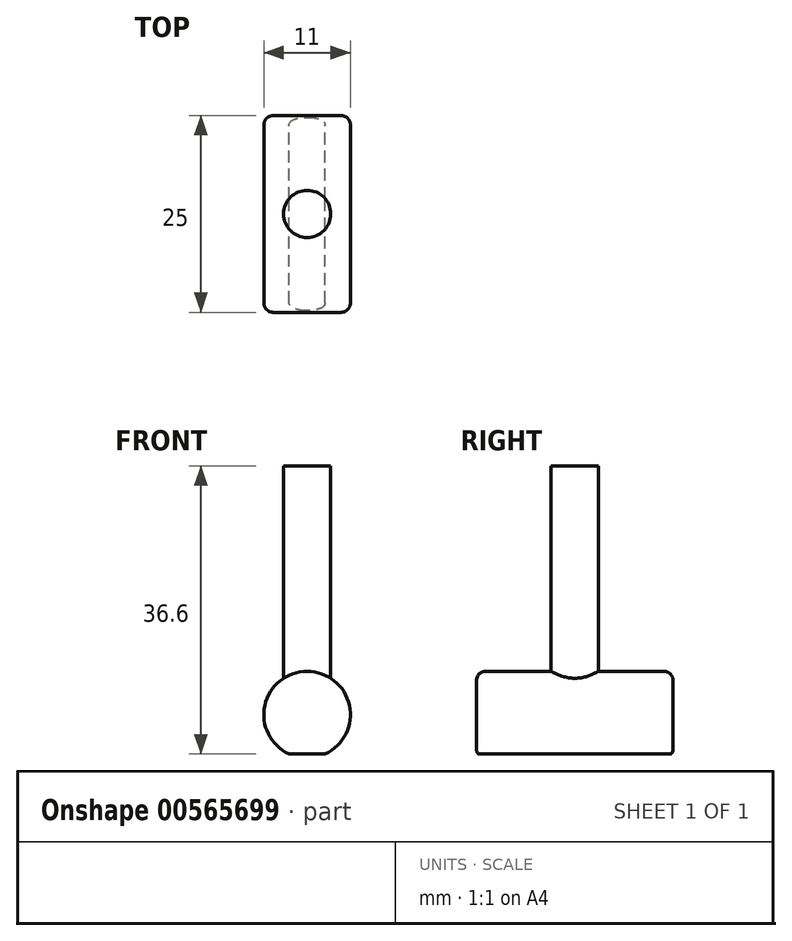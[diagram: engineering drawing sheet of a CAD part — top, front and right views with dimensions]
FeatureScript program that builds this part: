
annotation { "Feature Type Name" : "Feature", "Feature Type Description" : "" }
export const myFeature = defineFeature(function(context is Context, id is Id, definition is map)
    precondition{}
    {
        {
            var Q0;
            Q0=qCreatedBy(makeId("Front.planeOp"),FACE);
            var sketch = newSketch(context, id + "F0", { "sketchPlane" : qUnion([Q0])});
            skCircle(sketch, "E0", {"center": v(0, 0) * mm, "radius": 5.5 * mm});
            skSolve(sketch);
        }
        {
            var Q0;
            Q0 = qSketchRegion(id + "F0", true);
            extrude(context, id + "F1", {"entities" : qUnion([Q0]), "depth" : 25 * mm, "offsetDistance" : 25 * mm});
        }
        {
            var Q0;
            Q0=qCreatedBy(makeId("Front.planeOp"),FACE);
            var sketch = newSketch(context, id + "F2", { "sketchPlane" : qUnion([Q0])});
            skLineSegment(sketch, "E1", {"start": v(0, 11.6) * mm, "end": v(0, -5.5) * mm, "construction": true});
            skLineSegment(sketch, "E2.bottom", {"start": v(-2.3, -5) * mm, "end": v(2.3, -5) * mm});
            skLineSegment(sketch, "E2.top", {"start": v(-2.3, -5.5) * mm, "end": v(2.3, -5.5) * mm});
            skLineSegment(sketch, "E2.left", {"start": v(-2.3, -5) * mm, "end": v(-2.3, -5.5) * mm});
            skLineSegment(sketch, "E2.right", {"start": v(2.3, -5) * mm, "end": v(2.3, -5.5) * mm});
            skSolve(sketch);
        }
        {
            var Q0;
            Q0 = qSketchRegion(id + "F2", true);
            extrude(context, id + "F3", {"entities" : qUnion([Q0]), "operationType" : NewBodyOperationType.REMOVE, "endBound" : BoundingType.THROUGH_ALL, "depth" : 25 * mm, "offsetDistance" : 25 * mm});
        }
        {
            var Q0;
            Q0=sQuery(id+"F2.wireOp",VERTEX,"E1.start");
            var Q1;
            Q1=makeQuery(id+"F3.boolean.opBoolean","COPY",FACE,{"derivedFrom":makeQuery(id+"F3.opExtrude","SWEPT_FACE",FACE,{"disambiguationData":[OSD([sQuery(id+"F2.wireOp",EDGE,"E2.bottom")])]})});
            cPlane(context, id + "F4", {"entities" : qUnion([Q0, Q1]), "cplaneType" : CPlaneType.PLANE_POINT, "offset" : 25 * mm, "width" : 150 * mm, "height" : 150 * mm});
        }
        {
            var Q0;
            Q0=qCreatedBy(id+"F4.planeOp",FACE);
            var sketch = newSketch(context, id + "F5", { "sketchPlane" : qUnion([Q0])});
            skCircle(sketch, "E3", {"center": v(0, 12.5) * mm, "radius": 3 * mm});
            skLineSegment(sketch, "E4", {"start": v(0, 12.5) * mm, "end": v(0, 0) * mm, "construction": true});
            skLineSegment(sketch, "E5", {"start": v(0, 12.5) * mm, "end": v(0, 25) * mm, "construction": true});
            skSolve(sketch);
        }
        {
            var Q0;
            Q0 = qSketchRegion(id + "F5", true);
            var Q1;
            Q1=makeQuery(id+"F1.opExtrude","SWEPT_BODY",BODY,{"disambiguationData":[OSD([sQuery(id+"F0.wireOp",EDGE,"E0")])]});
            extrude(context, id + "F6", {"entities" : qUnion([Q0]), "operationType" : NewBodyOperationType.ADD, "endBound" : BoundingType.UP_TO_BODY, "depth" : 25 * mm, "endBoundEntityBody" : qUnion([Q1]), "offsetDistance" : 25 * mm, "hasSecondDirection" : true, "secondDirectionOppositeDirection" : true, "secondDirectionDepth" : 20 * mm});
        }
        {
            var Q0;
            Q0=makeQuery(id+"F1.opExtrude","CAP_EDGE",EDGE,{"disambiguationData":[OSD([sQuery(id+"F0.wireOp",EDGE,"E0")])],"isStart":false});
            var Q1;
            Q1=makeQuery(id+"F1.opExtrude","CAP_EDGE",EDGE,{"disambiguationData":[OSD([sQuery(id+"F0.wireOp",EDGE,"E0")])],"isStart":true});
            fillet(context, id + "F7", {"entities" : qUnion([Q0, Q1]), "radius" : 1.2 * mm, "tangentPropagation" : true, "allowEdgeOverflow" : false});
        }
    });
